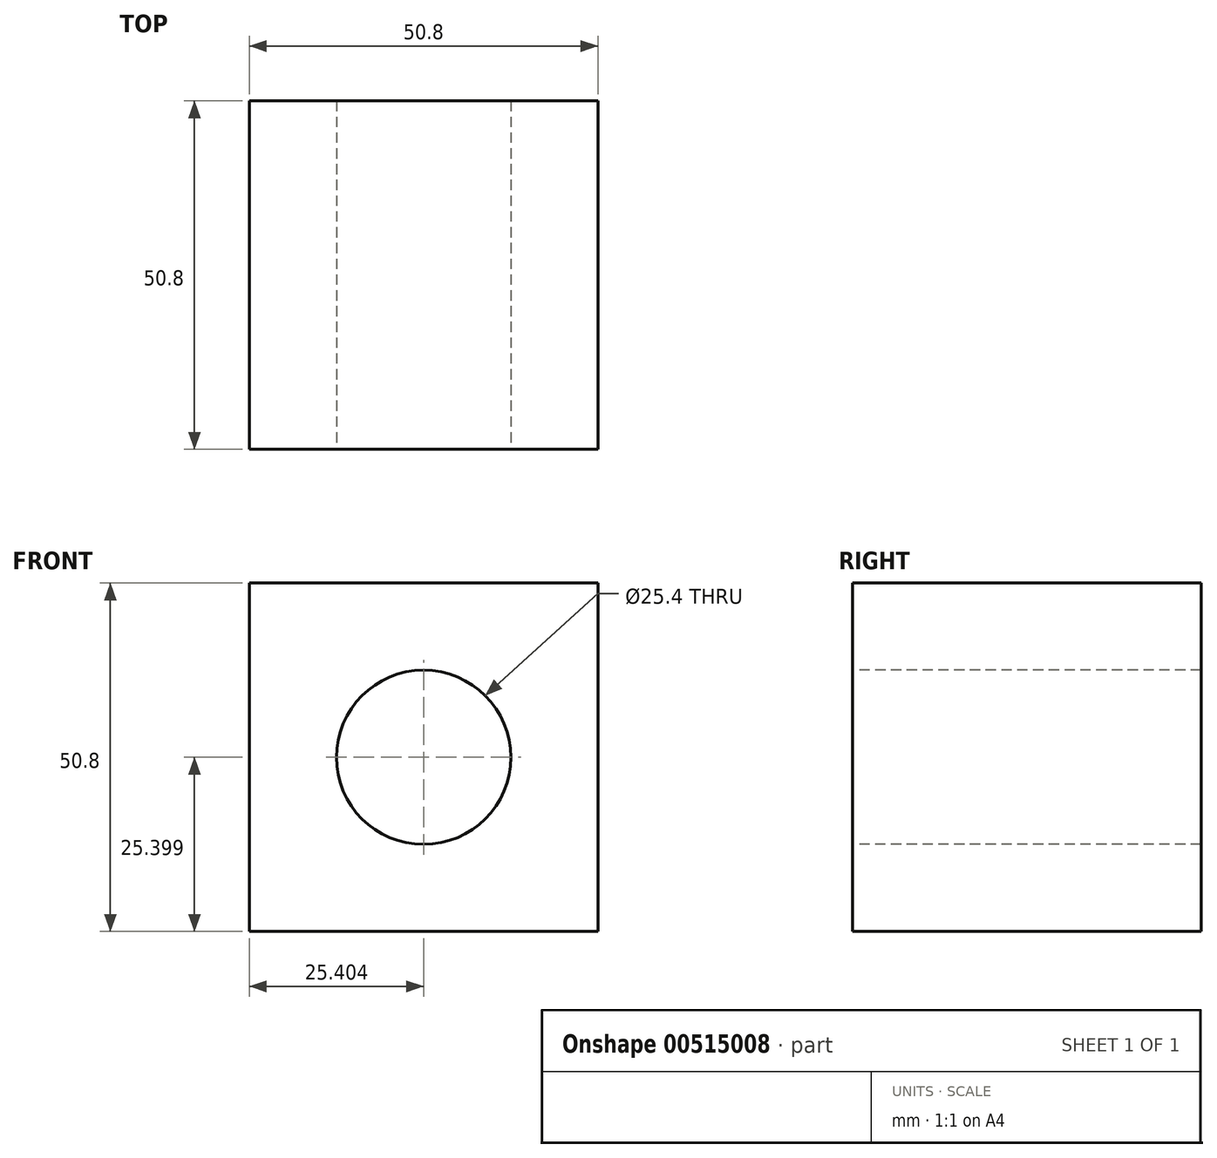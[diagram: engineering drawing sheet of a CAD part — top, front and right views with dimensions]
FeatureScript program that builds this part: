
annotation { "Feature Type Name" : "Feature", "Feature Type Description" : "" }
export const myFeature = defineFeature(function(context is Context, id is Id, definition is map)
    precondition{}
    {
        {
            var Q0;
            Q0=qCreatedBy(makeId("Front.planeOp"),FACE);
            var sketch = newSketch(context, id + "F0", { "sketchPlane" : qUnion([Q0])});
            skLineSegment(sketch, "E0.bottom", {"start": v(-47.94, 80.59) * mm, "end": v(2.86, 80.59) * mm});
            skLineSegment(sketch, "E0.top", {"start": v(-47.94, 29.79) * mm, "end": v(2.86, 29.79) * mm});
            skLineSegment(sketch, "E0.left", {"start": v(-47.94, 80.59) * mm, "end": v(-47.94, 29.79) * mm});
            skLineSegment(sketch, "E0.right", {"start": v(2.86, 80.59) * mm, "end": v(2.86, 29.79) * mm});
            skSolve(sketch);
        }
        {
            var Q0;
            Q0 = qSketchRegion(id + "F0", true);
            extrude(context, id + "F1", {"entities" : qUnion([Q0]), "depth" : 50.8 * mm, "offsetDistance" : 25.4 * mm});
        }
        {
            var Q0;
            Q0=makeQuery(id+"F1.opExtrude","CAP_FACE",FACE,{"disambiguationData":[OSD([sQuery(id+"F0.wireOp",EDGE,"E0.bottom"),sQuery(id+"F0.wireOp",EDGE,"E0.top"),sQuery(id+"F0.wireOp",EDGE,"E0.left"),sQuery(id+"F0.wireOp",EDGE,"E0.right")])],"isStart":false});
            var sketch = newSketch(context, id + "F2", { "sketchPlane" : qUnion([Q0])});
            skCircle(sketch, "E1", {"center": v(-22.54, 55.19) * mm, "radius": 12.7 * mm});
            skSolve(sketch);
        }
        {
            var Q0;
            Q0=makeQuery(id+"F2.imprint","IMPRINT",FACE,{"disambiguationData":[TD([[makeQuery(id+"F2.imprint","IMPRINT",EDGE,{"derivedFrom":sQuery(id+"F2.wireOp",EDGE,"E1")}),1.0]])]});
            extrude(context, id + "F3", {"entities" : qUnion([Q0]), "operationType" : NewBodyOperationType.REMOVE, "oppositeDirection" : true, "depth" : 50.8 * mm, "offsetDistance" : 25.4 * mm});
        }
    });
